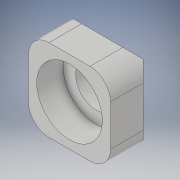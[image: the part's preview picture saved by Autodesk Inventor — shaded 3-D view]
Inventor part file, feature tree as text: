
AUTODESK INVENTOR PART (.ipt)
format: ipt  version: 2017 SP1 (Build 210196100, 196)  size: 131,072 bytes
history: native  units: in
note: dims shown in document units (in); Inventor stores cm internally (conversion verified against a paired STEP export)
features: sketch x2, extrude x1, hole x1, chamfer x1, fillet x1
ambient origin geometry x8: Origin, YZ Plane, XZ Plane, XY Plane, X Axis, Y Axis, Z Axis, Center Point
bodies: Solid1 (feature_tree)
feature tree (6):
  extrude  "Extrusion1"  Depth=0.5in
  hole  "Hole1"  [1 undecoded]
  chamfer  "Chamfer1"  Distance=0.125in
  fillet  "Fillet1"  [1 undecoded]
  sketch  "Sketch1"  dims[d0=0.5in d1=0.5in]
  sketch  "Sketch2"  dims[d2=0.25in d3=0.0in d4=0.25in d5=0.75in d6=0.4in d7=0.1625in d8=0.5635in d9=1.0in d10=0.8108in d11=0.05in d12=0.125in d13=45.0deg d14=0.125in]
note: 2 required parameter values undecoded (feature->parameter linkage not recoverable at this tier; creation-order binding heuristic only, values carry confidence <= 0.55)
